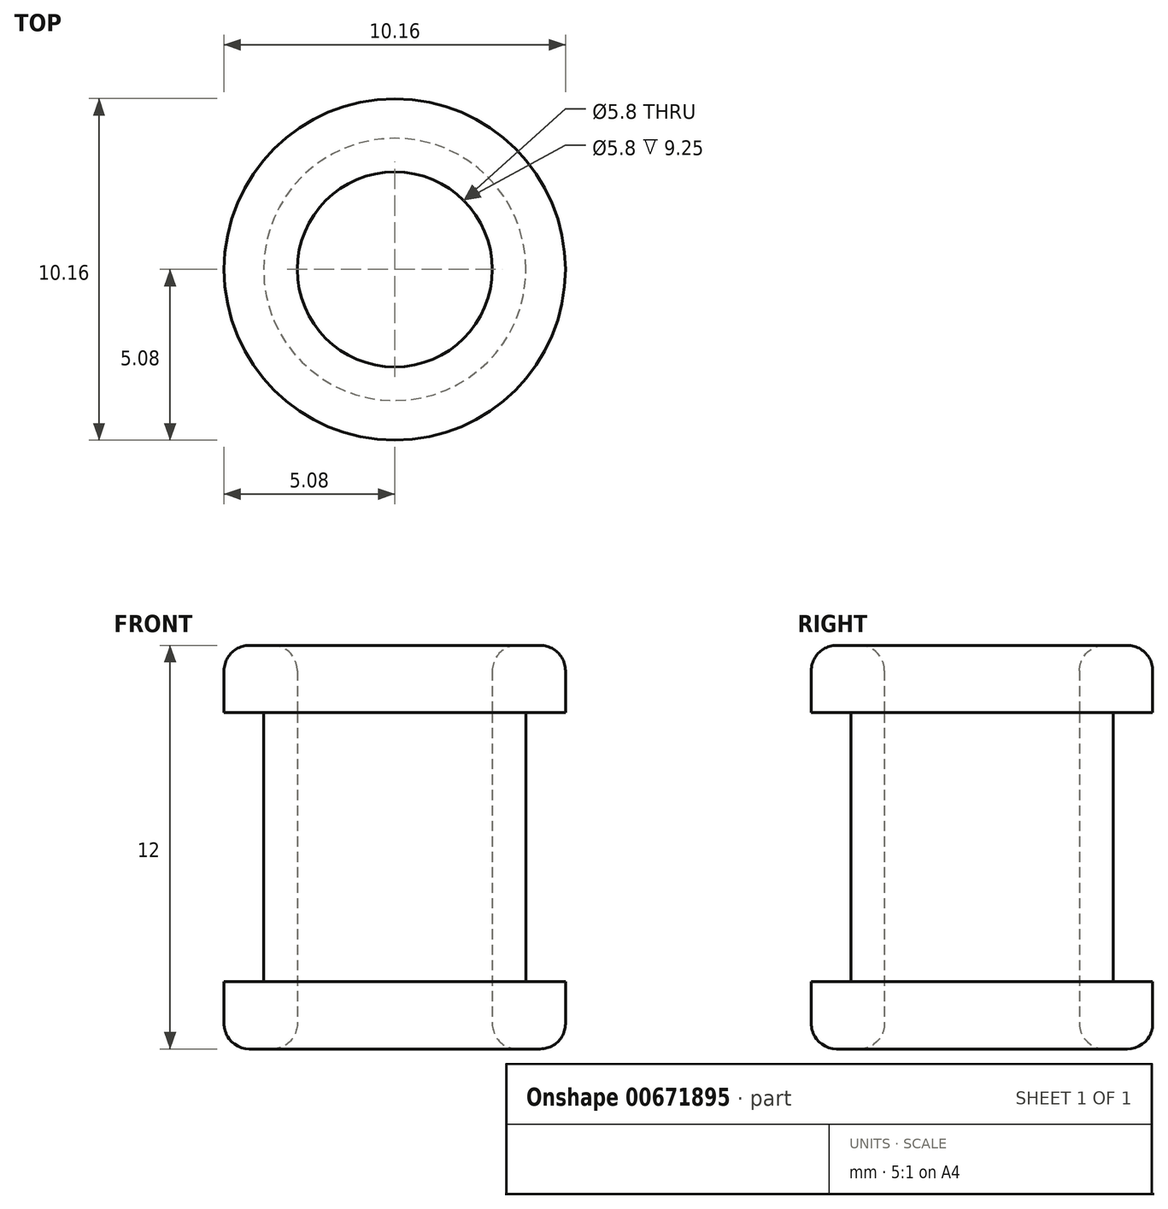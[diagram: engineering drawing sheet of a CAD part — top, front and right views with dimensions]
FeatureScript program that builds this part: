
annotation { "Feature Type Name" : "Feature", "Feature Type Description" : "" }
export const myFeature = defineFeature(function(context is Context, id is Id, definition is map)
    precondition{}
    {
        {
            var Q0;
            Q0=qCreatedBy(makeId("Top.planeOp"),FACE);
            var sketch = newSketch(context, id + "F0", { "sketchPlane" : qUnion([Q0])});
            skCircle(sketch, "E0", {"center": v(0, 0) * mm, "radius": 2.9 * mm});
            skCircle(sketch, "E1", {"center": v(0, 0) * mm, "radius": 3.9 * mm});
            skCircle(sketch, "E2", {"center": v(0, 0) * mm, "radius": 5.08 * mm});
            skSolve(sketch);
        }
        {
            var Q0;
            Q0=makeQuery(id+"F0.imprint","IMPRINT",FACE,{"disambiguationData":[TD([[makeQuery(id+"F0.imprint","IMPRINT",EDGE,{"derivedFrom":sQuery(id+"F0.wireOp",EDGE,"E0")}),-1.0]])]});
            extrude(context, id + "F1", {"entities" : qUnion([Q0]), "depth" : 10 * mm, "offsetDistance" : 25 * mm});
        }
        {
            var Q0;
            Q0=makeQuery(id+"F0.imprint","IMPRINT",FACE,{"disambiguationData":[TD([[makeQuery(id+"F0.imprint","IMPRINT",EDGE,{"derivedFrom":sQuery(id+"F0.wireOp",EDGE,"E1")}),-1.0]])]});
            extrude(context, id + "F2", {"entities" : qUnion([Q0]), "operationType" : NewBodyOperationType.ADD, "depth" : 2 * mm, "offsetDistance" : 25 * mm});
        }
        {
            var Q0;
            Q0=makeQuery(id+"F2.opExtrude","CAP_EDGE",EDGE,{"disambiguationData":[OSD([sQuery(id+"F0.wireOp",EDGE,"E2")])],"isStart":true});
            var Q1;
            Q1=makeQuery(id+"F1.opExtrude","CAP_EDGE",EDGE,{"disambiguationData":[OSD([sQuery(id+"F0.wireOp",EDGE,"E0")])],"isStart":true});
            fillet(context, id + "F3", {"entities" : qUnion([Q0, Q1]), "radius" : .75 * mm, "tangentPropagation" : true, "allowEdgeOverflow" : false});
        }
        {
            var Q0;
            Q0=makeQuery(id+"F1.opExtrude","CAP_FACE",FACE,{"disambiguationData":[OSD([sQuery(id+"F0.wireOp",EDGE,"E0"),sQuery(id+"F0.wireOp",EDGE,"E1")])],"isStart":false});
            var sketch = newSketch(context, id + "F4", { "sketchPlane" : qUnion([Q0])});
            skCircle(sketch, "E3", {"center": v(0, 0) * mm, "radius": 5.08 * mm});
            skSolve(sketch);
        }
        {
            var Q0;
            Q0=makeQuery(id+"F4.imprint","IMPRINT",FACE,{"disambiguationData":[TD([[makeQuery(id+"F4.imprint","IMPRINT",EDGE,{"derivedFrom":sQuery(id+"F4.wireOp",EDGE,"E3")}),1.0]])]});
            var Q1;
            Q1=makeQuery(id+"F4.imprint","IMPRINT",FACE,{"disambiguationData":[TD([[makeQuery(id+"F4.imprint","IMPRINT",EDGE,{"derivedFrom":makeQuery(id+"F1.opExtrude","CAP_EDGE",EDGE,{"disambiguationData":[OSD([sQuery(id+"F0.wireOp",EDGE,"E0")])],"isStart":false})}),-1.0]])]});
            extrude(context, id + "F5", {"entities" : qUnion([Q0, Q1]), "depth" : 2 * mm, "offsetDistance" : 25 * mm});
        }
        {
            var Q0;
            Q0=makeQuery(id+"F5.opExtrude","CAP_EDGE",EDGE,{"disambiguationData":[OSD([sQuery(id+"F4.wireOp",EDGE,"E3")])],"isStart":false});
            var Q1;
            Q1=makeQuery(id+"F5.opExtrude","CAP_EDGE",EDGE,{"disambiguationData":[OSD([sQuery(id+"F0.wireOp",EDGE,"E0")])],"isStart":false});
            fillet(context, id + "F6", {"entities" : qUnion([Q0, Q1]), "radius" : .75 * mm, "tangentPropagation" : true, "allowEdgeOverflow" : false});
        }
    });
